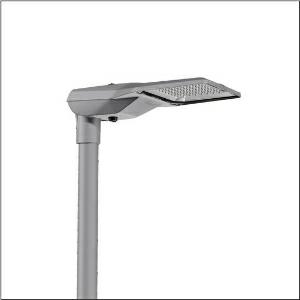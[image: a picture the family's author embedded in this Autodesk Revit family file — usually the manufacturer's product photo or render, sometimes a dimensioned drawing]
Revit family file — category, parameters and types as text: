
# Revit family: streetlight_sl_21_midi___stw1_0a_5xe3e23t08nb_45a6
name_source: partatom
category: Lighting Fixtures
units: mm (PartAtom-declared; Revit-internal decimal feet)

## family parameters
Cut with Voids When Loaded = No
Host = Face
Light Source = No
Part Type = Normal
Room Calculation Point = No
Round Connector Dimension = Use Diameter
Shared = No

## types (1)
- --- (1 x LED, 18780 lm, 151.2 W, 2200K)
    Apparent Load = 151 VA
    CIE Flux Codes = 39 75 98 100 100
    Color Rendering = 70
    Color Temperature = 2200K
    Default Elevation = 1800 mm
    Description = Streetlight SL 21 midi, mast luminaire, primary light control with lens, of PMMA, primary optical cover: cover, of toughened safety glass, transparent, light distribution: STW1.0a, light emission: direct distribution, primary light characteristic: asymmetric, installation type: side-entry, post-top, LED, High Power LED, rated luminous flux: 18.780lm, luminous efficacy: 124lm/W, light colour: 722, colour temperature: 2200K, control gear: D4i, control: overheat protection, constant luminous flux control, time-dependent luminous flux control, flexible luminous flux parameterisation, pre-setting: logarithmic dimming characteristic, mains connection: 230..240V, AC, 50/60Hz, start of lifetime: 151W, end of service life: 157W, reduction: 70W, luminaire housing, of diecast aluminium, powder-coated, SITECO metallic grey (DB 702S), corrosivity category C5 high according to DIN EN ISO 12944, please order mast flange separately, inclination adjustable: 0°, 5°, 10°, 15°, sealing non-destructively replaceable, multi-level sealing system, length: 644mm, width: 335mm, height: 110mm, mast flange for spigot size: 42mm (side-entry): 5XC10008XM4, 60/48mm (side-entry/post-top): 5XC10108XM2, 76/60mm (side-entry/post-top): 5XC10108XM1, mounting height: 4..8m, Smart Interface below and above, protection rating (complete): IP66, insulation class (complete): insulation class II (safety insulation), certification: CE, ENEC, ENEC+, VDE, impact resistance: IK10, permissible operating ambient temperature for outdoor applications: -40..+50°C, standard-compliant lighting for roads and squares, packaging unit: 1 piece

Light Distribution: STW1.0a
    Height = 111 mm
    Lamp = 1 x LED
    Lamp Light Flux = 18780 lm
    Lamp Power = 151.2 W
    Lamp count = 1
    Length = 644 mm
    Luminous efficacy = 124 lm/W
    Manufacturer = Siteco
    ModVariant = No
    Model = 5XE3E23T08NB
    Number of Poles = 1
    OnlyDefault = Yes
    Power Factor = 1
    Product Name = Streetlight SL 21 midi | STW1.0a
    Product group = mast luminaire | pylon top
    ProductGroupID = 6100
    Protection Class = Protection class II
    Protection Degree = IP 66
    RLX_Detail_Level = 1
    RLX_Emergency_Light_Flux = 0 lm
    RLX_Emergency_Type = 0
    RLX_Emergency_Type_DB = No
    RlxData = <blob elided: 27093 chars, md5=5b473a28>
    Socket = socket
    Standby Power = 0 W
    System Light Flux = 18781 lm
    System Power = 151 W
    Type Comments = factory setting: luminous flux: 100 % | dim-lin: 254 | 802 mA
    Type Image = l_1004304.jpg
    URL = http://relux.com
    VarID = @adj_169087
    Voltage = 0 V
    Weight = 0.00 kg
    Width = 336 mm

## geometry (parser evidence)
native form markers: Blend x4, Sweep x13
no freeform markers — native parametric forms only
